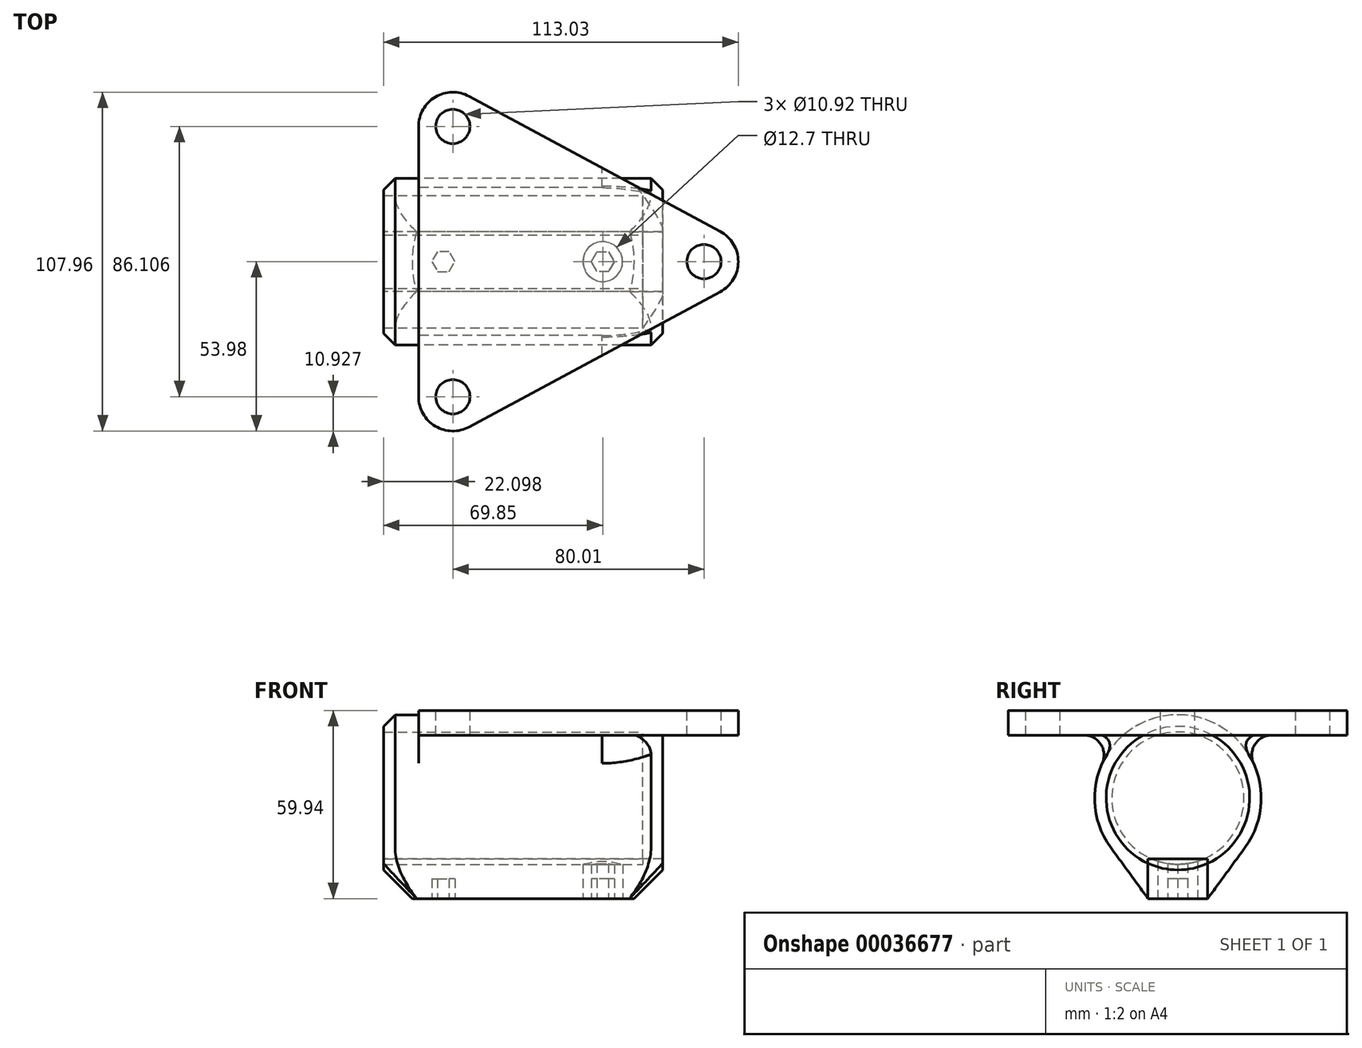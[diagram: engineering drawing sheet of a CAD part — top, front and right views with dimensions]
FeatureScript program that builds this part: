
annotation { "Feature Type Name" : "Feature", "Feature Type Description" : "" }
export const myFeature = defineFeature(function(context is Context, id is Id, definition is map)
    precondition{}
    {
        {
            var Q0;
            Q0=qCreatedBy(makeId("Right.planeOp"),FACE);
            var sketch = newSketch(context, id + "F0", { "sketchPlane" : qUnion([Q0])});
            skCircle(sketch, "E0", {"center": v(0, 0) * mm, "radius": 21.08 * mm});
            skCircle(sketch, "E1", {"center": v(0, 0) * mm, "radius": 26.54 * mm});
            skLineSegment(sketch, "E2.rect.top", {"start": v(9.53, -32) * mm, "end": v(-9.53, -32) * mm});
            skLineSegment(sketch, "E3", {"start": v(-9.52, -32) * mm, "end": v(-21.45, -15.63) * mm});
            skLineSegment(sketch, "E4", {"start": v(9.52, -32) * mm, "end": v(21.45, -15.63) * mm});
            skSolve(sketch);
        }
        {
            var Q0;
            Q0=makeQuery(id+"F0.imprint","IMPRINT",FACE,{"disambiguationData":[TD([[makeQuery(id+"F0.imprint","IMPRINT",EDGE,{"derivedFrom":sQuery(id+"F0.wireOp",EDGE,"E0")}),-1.0]])]});
            var Q1;
            Q1=makeQuery(id+"F0.imprint","IMPRINT",FACE,{"disambiguationData":[TD([[makeQuery(id+"F0.imprint","IMPRINT",EDGE,{"derivedFrom":sQuery(id+"F0.wireOp",EDGE,"E2.rect.top")}),-1.0]])]});
            var Q2;
            Q2=makeQuery(id+"F0.imprint","IMPRINT",FACE,{"disambiguationData":[TD([[makeQuery(id+"F0.imprint","IMPRINT",EDGE,{"derivedFrom":sQuery(id+"F0.wireOp",EDGE,"E0")}),1.0]])]});
            extrude(context, id + "F1", {"entities" : qUnion([Q0, Q1, Q2]), "endBound" : BoundingType.SYMMETRIC, "depth" : 88.9 * mm});
        }
        {
            var Q0;
            Q0=makeQuery(id+"F1.opExtrude","SWEPT_FACE",FACE,{"disambiguationData":[OSD([sQuery(id+"F0.wireOp",EDGE,"E2.rect.top")])]});
            var sketch = newSketch(context, id + "F2", { "sketchPlane" : qUnion([Q0])});
            skCircle(sketch, "E5", {"center": v(-25.4, 0) * mm, "radius": 6.35 * mm});
            skCircle(sketch, "E6.cCircle", {"center": v(-25.4, 0) * mm, "radius": 3.18 * mm, "construction": true});
            skLineSegment(sketch, "E6.0", {"start": v(-27.23, 3.18) * mm, "end": v(-23.57, 3.18) * mm});
            skLineSegment(sketch, "E6.1", {"start": v(-23.57, 3.17) * mm, "end": v(-21.73, 0) * mm});
            skLineSegment(sketch, "E6.2", {"start": v(-21.73, 0) * mm, "end": v(-23.57, -3.18) * mm});
            skLineSegment(sketch, "E6.3", {"start": v(-23.57, -3.17) * mm, "end": v(-27.23, -3.17) * mm});
            skLineSegment(sketch, "E6.4", {"start": v(-27.23, -3.18) * mm, "end": v(-29.07, 0) * mm});
            skLineSegment(sketch, "E6.5", {"start": v(-29.07, 0) * mm, "end": v(-27.23, 3.18) * mm});
            skPoint(sketch, "E6.0.midPoint", {"position": v(-25.4, 3.18) * mm});
            skCircle(sketch, "E7.MirrorC", {"center": v(25.4, 0) * mm, "radius": 6.35 * mm});
            skLineSegment(sketch, "E8.MirrorCS", {"start": v(27.23, 3.17) * mm, "end": v(23.57, 3.17) * mm});
            skLineSegment(sketch, "E9.MirrorCS", {"start": v(23.57, 3.17) * mm, "end": v(21.73, 0) * mm});
            skLineSegment(sketch, "E10.MirrorCS", {"start": v(21.73, 0) * mm, "end": v(23.57, -3.18) * mm});
            skLineSegment(sketch, "E11.MirrorCS", {"start": v(23.57, -3.18) * mm, "end": v(27.23, -3.18) * mm});
            skLineSegment(sketch, "E12.MirrorCS", {"start": v(27.23, -3.18) * mm, "end": v(29.07, 0) * mm});
            skLineSegment(sketch, "E13.MirrorCS", {"start": v(29.07, 0) * mm, "end": v(27.23, 3.18) * mm});
            skSolve(sketch);
        }
        {
            var Q0;
            Q0=makeQuery(id+"F2.imprint","IMPRINT",FACE,{"disambiguationData":[TD([[makeQuery(id+"F2.imprint","IMPRINT",EDGE,{"derivedFrom":sQuery(id+"F2.wireOp",EDGE,"E6.0")}),-1.0]])]});
            var Q1;
            Q1=makeQuery(id+"F2.imprint","IMPRINT",FACE,{"disambiguationData":[TD([[makeQuery(id+"F2.imprint","IMPRINT",EDGE,{"derivedFrom":sQuery(id+"F2.wireOp",EDGE,"E5")}),1.0]])]});
            var Q2;
            Q2=makeQuery(id+"F2.imprint","IMPRINT",FACE,{"disambiguationData":[TD([[makeQuery(id+"F2.imprint","IMPRINT",EDGE,{"derivedFrom":sQuery(id+"F2.wireOp",EDGE,"E8.MirrorCS")}),1.0]])]});
            var Q3;
            Q3=makeQuery(id+"F2.imprint","IMPRINT",FACE,{"disambiguationData":[TD([[makeQuery(id+"F2.imprint","IMPRINT",EDGE,{"derivedFrom":sQuery(id+"F2.wireOp",EDGE,"E7.MirrorC")}),-1.0]])]});
            extrude(context, id + "F3", {"entities" : qUnion([Q0, Q1, Q2, Q3]), "oppositeDirection" : true, "depth" : 12.7 * mm});
        }
        {
            var Q0;
            Q0=makeQuery(id+"F3.opExtrude","SWEPT_BODY",BODY,{"disambiguationData":[OSD([sQuery(id+"F2.wireOp",EDGE,"E5")])]});
            var Q1;
            Q1=makeQuery(id+"F3.opExtrude","SWEPT_BODY",BODY,{"disambiguationData":[OSD([sQuery(id+"F2.wireOp",EDGE,"E7.MirrorC")])]});
            var Q2;
            Q2=makeQuery(id+"FDmkU0JhcyfajZN_1.opExtrude","SWEPT_BODY",BODY,{"disambiguationData":[OSD([sQuery(id+"Fau4lb0L3iw3XX0_1.wireOp",EDGE,"aa76d7ee-a35b-4488-8276-169a7f60b04d")])]});
            var Q3;
            Q3=makeQuery(id+"F1.opExtrude","SWEPT_BODY",BODY,{"disambiguationData":[OSD([sQuery(id+"F0.wireOp",EDGE,"E1"),sQuery(id+"F0.wireOp",EDGE,"E2.rect.bottom"),sQuery(id+"F0.wireOp",EDGE,"E2.rect.top"),sQuery(id+"F0.wireOp",EDGE,"a51bb4f6-294f-47ed-b473-a52ab50b22ea"),sQuery(id+"F0.wireOp",EDGE,"8497208a-9e24-4526-a7f4-8772f674d511"),sQuery(id+"F0.wireOp",EDGE,"E3"),sQuery(id+"F0.wireOp",EDGE,"E4")])]});
            booleanBodies(context, id + "F4", {"operationType" : BooleanOperationType.SUBTRACTION, "tools" : qUnion([Q0, Q1, Q2]), "targets" : qUnion([Q3]), "keepTools" : true});
        }
        {
            var Q0;
            Q0=makeQuery(id+"F2.imprint","IMPRINT",FACE,{"disambiguationData":[TD([[makeQuery(id+"F2.imprint","IMPRINT",EDGE,{"derivedFrom":sQuery(id+"F2.wireOp",EDGE,"E6.0")}),-1.0]])]});
            var Q1;
            Q1=makeQuery(id+"F2.imprint","IMPRINT",FACE,{"disambiguationData":[TD([[makeQuery(id+"F2.imprint","IMPRINT",EDGE,{"derivedFrom":sQuery(id+"F2.wireOp",EDGE,"E8.MirrorCS")}),1.0]])]});
            extrude(context, id + "F5", {"entities" : qUnion([Q0, Q1]), "operationType" : NewBodyOperationType.REMOVE, "oppositeDirection" : true, "depth" : 6.35 * mm});
        }
        {
            var Q0;
            Q0=qCreatedBy(makeId("Front.planeOp"),FACE);
            var sketch = newSketch(context, id + "F6", { "sketchPlane" : qUnion([Q0])});
            skLineSegment(sketch, "E14", {"start": v(-67.31, 0) * mm, "end": v(-29.2, 38.1) * mm});
            skLineSegment(sketch, "E15", {"start": v(-29.21, 38.1) * mm, "end": v(-73.66, 38.1) * mm});
            skLineSegment(sketch, "E16", {"start": v(-73.66, 38.1) * mm, "end": v(-73.66, 0) * mm});
            skLineSegment(sketch, "E17", {"start": v(-73.66, 0) * mm, "end": v(-67.31, 0) * mm});
            skLineSegment(sketch, "E18.MirrorCS", {"start": v(67.31, 0) * mm, "end": v(29.2, 38.1) * mm});
            skLineSegment(sketch, "E19.MirrorCS", {"start": v(29.21, 38.1) * mm, "end": v(73.66, 38.1) * mm});
            skLineSegment(sketch, "E20.MirrorCS", {"start": v(73.66, 0) * mm, "end": v(67.31, 0) * mm});
            skLineSegment(sketch, "E21.MirrorCS", {"start": v(73.66, 38.1) * mm, "end": v(73.66, 0) * mm});
            skSolve(sketch);
        }
        {
            var Q0;
            Q0=makeQuery(id+"F6.imprint","IMPRINT",FACE,{"disambiguationData":[TD([[makeQuery(id+"F6.imprint","IMPRINT",EDGE,{"derivedFrom":sQuery(id+"F6.wireOp",EDGE,"E14")}),1.0]])]});
            var Q1;
            Q1=makeQuery(id+"F6.imprint","IMPRINT",FACE,{"disambiguationData":[TD([[makeQuery(id+"F6.imprint","IMPRINT",EDGE,{"derivedFrom":sQuery(id+"F6.wireOp",EDGE,"E18.MirrorCS")}),-1.0]])]});
            var Q2;
            Q2=sQuery(id+"F6.wireOp",EDGE,"E17");
            revolve(context, id + "F7", {"operationType" : NewBodyOperationType.REMOVE, "entities" : qUnion([Q0, Q1]), "axis" : qUnion([Q2]), "revolveType" : RevolveType.FULL, "oppositeDirection" : true});
        }
        {
            var Q0;
            Q0=qCreatedBy(makeId("Top.planeOp"),FACE);
            cPlane(context, id + "F8", {"entities" : qUnion([Q0]), "cplaneType" : CPlaneType.OFFSET, "offset" : 27.94 * mm, "width" : 152.4 * mm, "height" : 152.4 * mm});
        }
        {
            var Q0;
            Q0=qCreatedBy(id+"F8.planeOp",FACE);
            var sketch = newSketch(context, id + "F9", { "sketchPlane" : qUnion([Q0])});
            skLineSegment(sketch, "E22", {"start": v(57.66, 0) * mm, "end": v(-22.35, -43.05) * mm, "construction": true});
            skLineSegment(sketch, "E23", {"start": v(-22.35, -43.05) * mm, "end": v(-22.35, 43.05) * mm, "construction": true});
            skLineSegment(sketch, "E24", {"start": v(-22.35, 43.05) * mm, "end": v(57.66, 0) * mm, "construction": true});
            skCircle(sketch, "E25", {"center": v(-22.35, 43.05) * mm, "radius": 5.46 * mm});
            skCircle(sketch, "E26", {"center": v(-22.35, -43.05) * mm, "radius": 5.46 * mm});
            skCircle(sketch, "E27", {"center": v(57.66, 0) * mm, "radius": 5.46 * mm});
            skCircle(sketch, "E28", {"center": v(57.66, 0) * mm, "radius": 10.92 * mm});
            skCircle(sketch, "E29", {"center": v(-22.35, -43.05) * mm, "radius": 10.92 * mm});
            skCircle(sketch, "E30", {"center": v(-22.35, 43.05) * mm, "radius": 10.92 * mm});
            skLineSegment(sketch, "E31", {"start": v(-17.18, 52.67) * mm, "end": v(62.83, 9.62) * mm});
            skLineSegment(sketch, "E32", {"start": v(-33.27, 43.05) * mm, "end": v(-33.27, -43.05) * mm});
            skLineSegment(sketch, "E33", {"start": v(-17.18, -52.67) * mm, "end": v(62.83, -9.62) * mm});
            skSolve(sketch);
        }
        {
            var Q0;
            {var subQ2=sQuery(id+"F9.wireOp",EDGE,"E31");Q0=makeQuery(id+"F9.imprint","IMPRINT",FACE,{"disambiguationData":[TD([[makeQuery(id+"F9.imprint","IMPRINT",EDGE,{"derivedFrom":subQ2}),-1.0]])]});}
            var Q1;
            Q1=makeQuery(id+"F9.imprint","IMPRINT",FACE,{"disambiguationData":[TD([[makeQuery(id+"F9.imprint","IMPRINT",EDGE,{"derivedFrom":sQuery(id+"F9.wireOp",EDGE,"E25")}),-1.0]])]});
            var Q2;
            Q2=makeQuery(id+"F9.imprint","IMPRINT",FACE,{"disambiguationData":[TD([[makeQuery(id+"F9.imprint","IMPRINT",EDGE,{"derivedFrom":sQuery(id+"F9.wireOp",EDGE,"E26")}),-1.0]])]});
            var Q3;
            Q3=makeQuery(id+"F9.imprint","IMPRINT",FACE,{"disambiguationData":[TD([[makeQuery(id+"F9.imprint","IMPRINT",EDGE,{"derivedFrom":sQuery(id+"F9.wireOp",EDGE,"E27")}),-1.0]])]});
            extrude(context, id + "F10", {"entities" : qUnion([Q0, Q1, Q2, Q3]), "operationType" : NewBodyOperationType.ADD, "oppositeDirection" : true, "depth" : 7.87 * mm});
        }
        {
            var Q0;
            Q0=makeQuery(id+"F0.imprint","IMPRINT",FACE,{"disambiguationData":[TD([[makeQuery(id+"F0.imprint","IMPRINT",EDGE,{"derivedFrom":sQuery(id+"F0.wireOp",EDGE,"E0")}),1.0]])]});
            extrude(context, id + "F11", {"entities" : qUnion([Q0]), "operationType" : NewBodyOperationType.REMOVE, "endBound" : BoundingType.THROUGH_ALL, "oppositeDirection" : true, "depth" : 25.4 * mm, "hasSecondDirection" : true, "secondDirectionOppositeDirection" : false, "secondDirectionDepth" : 38.1 * mm});
        }
        {
            var Q0;
            Q0=makeQuery(id+"F10.boolean.opBoolean","INTERSECT",EDGE,{"disambiguationData":[OD(1.0)],"derivedFrom":[makeQuery(id+"F1.opExtrude","SWEPT_FACE",FACE,{"disambiguationData":[OSD([sQuery(id+"F0.wireOp",EDGE,"E1")])]}),makeQuery(id+"F10.opExtrude","CAP_FACE",FACE,{"disambiguationData":[OSD([sQuery(id+"F9.wireOp",EDGE,"E25"),sQuery(id+"F9.wireOp",EDGE,"E26"),sQuery(id+"F9.wireOp",EDGE,"E27"),sQuery(id+"F9.wireOp",EDGE,"E28"),sQuery(id+"F9.wireOp",EDGE,"E29"),sQuery(id+"F9.wireOp",EDGE,"E30"),sQuery(id+"F9.wireOp",EDGE,"E31"),sQuery(id+"F9.wireOp",EDGE,"E32"),sQuery(id+"F9.wireOp",EDGE,"E33")])],"isStart":false})]});
            var Q1;
            Q1=makeQuery(id+"F10.boolean.opBoolean","INTERSECT",EDGE,{"disambiguationData":[OD(0.0)],"derivedFrom":[makeQuery(id+"F1.opExtrude","SWEPT_FACE",FACE,{"disambiguationData":[OSD([sQuery(id+"F0.wireOp",EDGE,"E1")])]}),makeQuery(id+"F10.opExtrude","CAP_FACE",FACE,{"disambiguationData":[OSD([sQuery(id+"F9.wireOp",EDGE,"E25"),sQuery(id+"F9.wireOp",EDGE,"E26"),sQuery(id+"F9.wireOp",EDGE,"E27"),sQuery(id+"F9.wireOp",EDGE,"E28"),sQuery(id+"F9.wireOp",EDGE,"E29"),sQuery(id+"F9.wireOp",EDGE,"E30"),sQuery(id+"F9.wireOp",EDGE,"E31"),sQuery(id+"F9.wireOp",EDGE,"E32"),sQuery(id+"F9.wireOp",EDGE,"E33")])],"isStart":false})]});
            fillet(context, id + "F12", {"entities" : qUnion([Q0, Q1]), "radius" : 6.35 * mm, "tangentPropagation" : true, "allowEdgeOverflow" : false});
        }
    });
